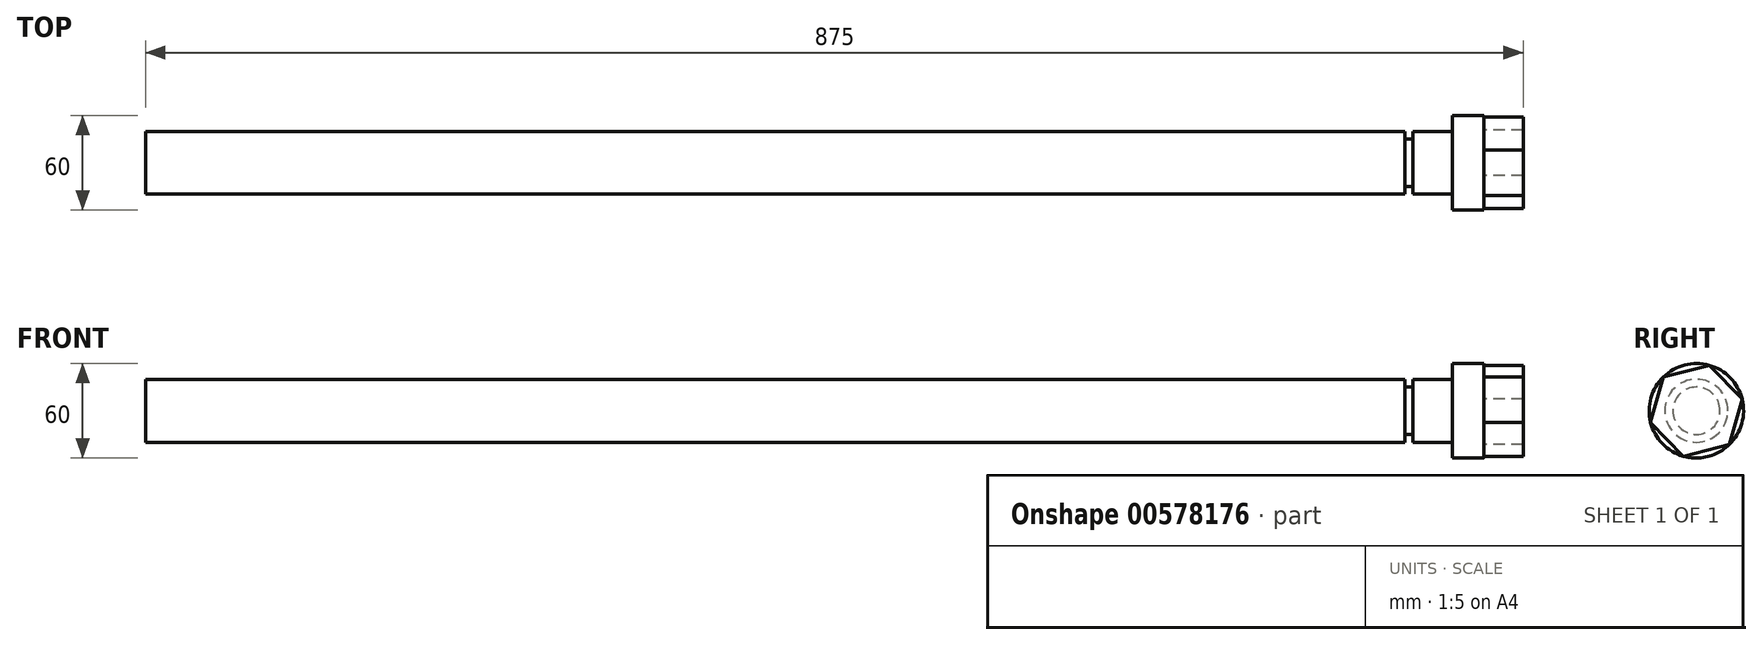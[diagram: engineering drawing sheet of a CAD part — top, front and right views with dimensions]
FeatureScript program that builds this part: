
annotation { "Feature Type Name" : "Feature", "Feature Type Description" : "" }
export const myFeature = defineFeature(function(context is Context, id is Id, definition is map)
    precondition{}
    {
        {
            var Q0;
            Q0=qCreatedBy(makeId("Front.planeOp"),FACE);
            var sketch = newSketch(context, id + "F0", { "sketchPlane" : qUnion([Q0])});
            skLineSegment(sketch, "E0", {"start": v(425, 0) * mm, "end": v(-425, 0) * mm});
            skLineSegment(sketch, "E1", {"start": v(-425, 0) * mm, "end": v(-425, 20) * mm});
            skLineSegment(sketch, "E2", {"start": v(-425, 20) * mm, "end": v(375, 20) * mm});
            skLineSegment(sketch, "E3", {"start": v(375, 20) * mm, "end": v(375, 15) * mm});
            skLineSegment(sketch, "E4", {"start": v(375, 15) * mm, "end": v(380, 15) * mm});
            skLineSegment(sketch, "E5", {"start": v(380, 15) * mm, "end": v(380, 20) * mm});
            skLineSegment(sketch, "E6", {"start": v(380, 20) * mm, "end": v(405, 20) * mm});
            skLineSegment(sketch, "E7", {"start": v(405, 20) * mm, "end": v(405, 30) * mm});
            skLineSegment(sketch, "E8", {"start": v(405, 30) * mm, "end": v(425, 30) * mm});
            skLineSegment(sketch, "E9", {"start": v(425, 30) * mm, "end": v(425, 0) * mm});
            skLineSegment(sketch, "E10", {"start": v(489.38, 0) * mm, "end": v(-511.64, 0) * mm, "construction": true});
            skSolve(sketch);
        }
        {
            var Q0;
            Q0=makeQuery(id+"F0.imprint","IMPRINT",FACE,{"disambiguationData":[TD([[makeQuery(id+"F0.imprint","IMPRINT",EDGE,{"derivedFrom":sQuery(id+"F0.wireOp",EDGE,"E0")}),-1.0]])]});
            var Q1;
            Q1=sQuery(id+"F0.wireOp",EDGE,"E10");
            revolve(context, id + "F1", {"entities" : qUnion([Q0]), "axis" : qUnion([Q1]), "revolveType" : RevolveType.FULL});
        }
        {
            var Q0;
            Q0=makeQuery(id+"F1.opRevolve","SWEPT_FACE",FACE,{"disambiguationData":[OSD([sQuery(id+"F0.wireOp",EDGE,"E9")])]});
            var sketch = newSketch(context, id + "F2", { "sketchPlane" : qUnion([Q0])});
            skCircle(sketch, "E11.0.0", {"center": v(0, 0) * mm, "radius": 30 * mm});
            skCircle(sketch, "E12.cCircle", {"center": v(0, 0) * mm, "radius": 30 * mm, "construction": true});
            skLineSegment(sketch, "E12.0", {"start": v(20.93, -21.5) * mm, "end": v(-8.15, -28.87) * mm});
            skLineSegment(sketch, "E12.1", {"start": v(-8.15, -28.87) * mm, "end": v(-29.08, -7.38) * mm});
            skLineSegment(sketch, "E12.2", {"start": v(-29.08, -7.38) * mm, "end": v(-20.93, 21.5) * mm});
            skLineSegment(sketch, "E12.3", {"start": v(-20.93, 21.5) * mm, "end": v(8.15, 28.87) * mm});
            skLineSegment(sketch, "E12.4", {"start": v(8.15, 28.87) * mm, "end": v(29.08, 7.38) * mm});
            skLineSegment(sketch, "E12.5", {"start": v(29.08, 7.38) * mm, "end": v(20.93, -21.5) * mm});
            skSolve(sketch);
        }
        {
            var Q0;
            Q0=makeQuery(id+"F2.imprint","IMPRINT",FACE,{"disambiguationData":[TD([[makeQuery(id+"F2.imprint","IMPRINT",EDGE,{"derivedFrom":sQuery(id+"F2.wireOp",EDGE,"E12.0")}),-1.0]])]});
            extrude(context, id + "F3", {"entities" : qUnion([Q0]), "operationType" : NewBodyOperationType.ADD, "depth" : 25 * mm, "offsetDistance" : 25 * mm});
        }
    });
